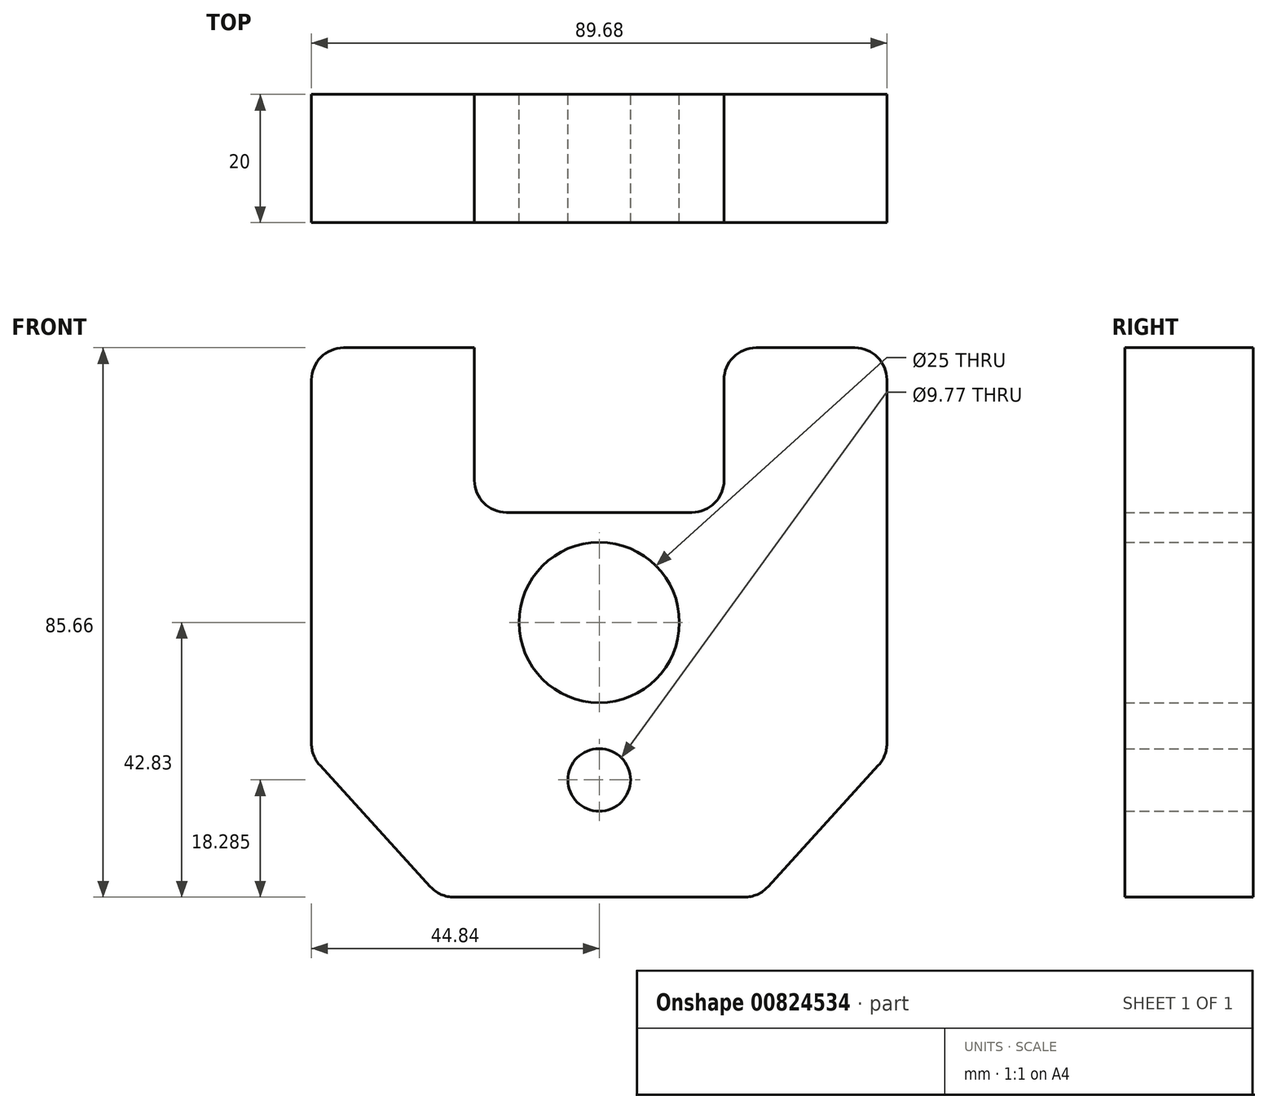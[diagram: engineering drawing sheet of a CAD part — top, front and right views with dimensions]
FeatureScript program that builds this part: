
annotation { "Feature Type Name" : "Feature", "Feature Type Description" : "" }
export const myFeature = defineFeature(function(context is Context, id is Id, definition is map)
    precondition{}
    {
        {
            var Q0;
            Q0=qCreatedBy(makeId("Front.planeOp"),FACE);
            var sketch = newSketch(context, id + "F0", { "sketchPlane" : qUnion([Q0])});
            skLineSegment(sketch, "E0.bottom", {"start": v(24.84, -42.83) * mm, "end": v(-24.84, -42.83) * mm});
            skLineSegment(sketch, "E0.top", {"start": v(44.84, 42.83) * mm, "end": v(19.45, 42.83) * mm});
            skLineSegment(sketch, "E0.left", {"start": v(44.84, -20.83) * mm, "end": v(44.84, 42.83) * mm});
            skLineSegment(sketch, "E0.right", {"start": v(-44.84, -20.83) * mm, "end": v(-44.84, 42.83) * mm});
            skPoint(sketch, "E0.middle", {"position": v(0, 0) * mm});
            skCircle(sketch, "E1", {"center": v(0, 0) * mm, "radius": 12.5 * mm});
            skLineSegment(sketch, "E2", {"start": v(-19.45, 42.83) * mm, "end": v(-19.45, 22.17) * mm});
            skLineSegment(sketch, "E3", {"start": v(-14.45, 17.17) * mm, "end": v(14.45, 17.17) * mm});
            skLineSegment(sketch, "E4", {"start": v(19.45, 22.17) * mm, "end": v(19.45, 42.83) * mm});
            skLineSegment(sketch, "E5.trimOffspring", {"start": v(-19.45, 42.83) * mm, "end": v(-44.84, 42.83) * mm});
            skPoint(sketch, "E6.visualSharp", {"position": v(-19.45, 17.17) * mm});
            skArc(sketch, "E6.filletArc", {"start": v(-19.45, 22.17) * mm, "mid": v(-17.99, 18.63) * mm, "end": v(-14.45, 17.17) * mm});
            skPoint(sketch, "E7.visualSharp", {"position": v(19.45, 17.17) * mm});
            skArc(sketch, "E7.filletArc", {"start": v(14.45, 17.17) * mm, "mid": v(17.99, 18.63) * mm, "end": v(19.45, 22.17) * mm});
            skLineSegment(sketch, "E8", {"start": v(-44.84, -20.83) * mm, "end": v(-24.84, -42.83) * mm});
            skPoint(sketch, "E9.orphan", {"position": v(-44.84, -42.83) * mm});
            skLineSegment(sketch, "E10", {"start": v(24.84, -42.83) * mm, "end": v(44.84, -20.83) * mm});
            skPoint(sketch, "E11.orphan", {"position": v(44.84, -42.83) * mm});
            skCircle(sketch, "E12", {"center": v(0, -24.54) * mm, "radius": 4.88 * mm});
            skSolve(sketch);
        }
        {
            var Q0;
            Q0=makeQuery(id+"F0.imprint","IMPRINT",FACE,{"disambiguationData":[TD([[makeQuery(id+"F0.imprint","IMPRINT",EDGE,{"derivedFrom":sQuery(id+"F0.wireOp",EDGE,"E0.bottom")}),-1.0]])]});
            extrude(context, id + "F1", {"entities" : qUnion([Q0]), "depth" : 20 * mm, "offsetDistance" : 25 * mm});
        }
        {
            var Q0;
            Q0=makeQuery(id+"F1.opExtrude","SWEPT_EDGE",EDGE,{"disambiguationData":[OSD([sQuery(id+"F0.wireOp",EDGE,"E0.top"),sQuery(id+"F0.wireOp",EDGE,"E0.left")])]});
            var Q1;
            Q1=makeQuery(id+"F1.opExtrude","SWEPT_EDGE",EDGE,{"disambiguationData":[OSD([sQuery(id+"F0.wireOp",EDGE,"E0.bottom"),sQuery(id+"F0.wireOp",EDGE,"E0.right")])]});
            var Q2;
            Q2=makeQuery(id+"F1.opExtrude","SWEPT_EDGE",EDGE,{"disambiguationData":[OSD([sQuery(id+"F0.wireOp",EDGE,"E0.bottom"),sQuery(id+"F0.wireOp",EDGE,"E0.left")])]});
            var Q3;
            Q3=makeQuery(id+"F1.opExtrude","SWEPT_EDGE",EDGE,{"disambiguationData":[OSD([sQuery(id+"F0.wireOp",EDGE,"E0.top"),sQuery(id+"F0.wireOp",EDGE,"E0.right")])]});
            fillet(context, id + "F2", {"entities" : qUnion([Q0, Q1, Q2, Q3]), "radius" : 5 * mm, "tangentPropagation" : true, "allowEdgeOverflow" : false});
        }
    });
